FCSTD DOCUMENT  (FreeCAD 0.21R33694 (Git))
Label: home-center-line-measurement
License: All rights reserved
LicenseURL: http://en.wikipedia.org/wiki/All_rights_reserved
objects: Sketcher::SketchObject×1, PartDesign::Body×1
note: 2 computed .brp shape members not serialized (recipe doc carries the construction recipe); baked Part::Feature solids carry a one-line shape summary decoded from their .brp

FEATURE [Sketcher::SketchObject] Sketch
  FullyConstrained = false
  MapMode = 5
  Support = -> [XY_Plane]
  sketch-geometry (7):
    g0: LineSegment StartX=0 StartY=-3.188e-13 StartZ=0 EndX=9.49955 EndY=43.7542 EndZ=0
    g1: LineSegment StartX=9.49955 StartY=43.7542 StartZ=0 EndX=87.9906 EndY=38.0047 EndZ=0
    g2: LineSegment StartX=87.9906 StartY=38.0047 StartZ=0 EndX=85.725 EndY=-12.7 EndZ=0
    g3: LineSegment StartX=85.725 StartY=-12.7 StartZ=0 EndX=0 EndY=-3.18e-13 EndZ=0
    g4: LineSegment StartX=85.725 StartY=-12.7 StartZ=0 EndX=0 EndY=-12.7 EndZ=0
    g5: LineSegment StartX=9.49955 StartY=43.7542 StartZ=0 EndX=9.95e-14 EndY=44.45 EndZ=0
    g6: LineSegment StartX=9.88e-14 StartY=44.45 StartZ=0 EndX=0 EndY=-12.7 EndZ=0
  constraints (17):
    c: Coincident(g-1,g0)
    c: Coincident(g0,g1)
    c: Coincident(g1,g2)
    c: Coincident(g2,g3)
    c: Coincident(g3,g0)
    c: Coincident(g4,g2)
    c: PointOnObject(g4,g-2)
    c: Horizontal(g4)
    c: Coincident(g5,g0)
    c: PointOnObject(g5,g-2)
    c: Parallel(g5,g1)
    c: Coincident(g6,g5)
    c: Coincident(g6,g4)
    c: Distance(g5) = 9.525
    c: Distance(g4) = 85.725
    c: Distance(g0,g4) = 12.7
    c: DistanceY(g4,g5) = 57.15
FEATURE [PartDesign::Body] Body
  Group = -> [Sketch]
  Origin = -> Origin
